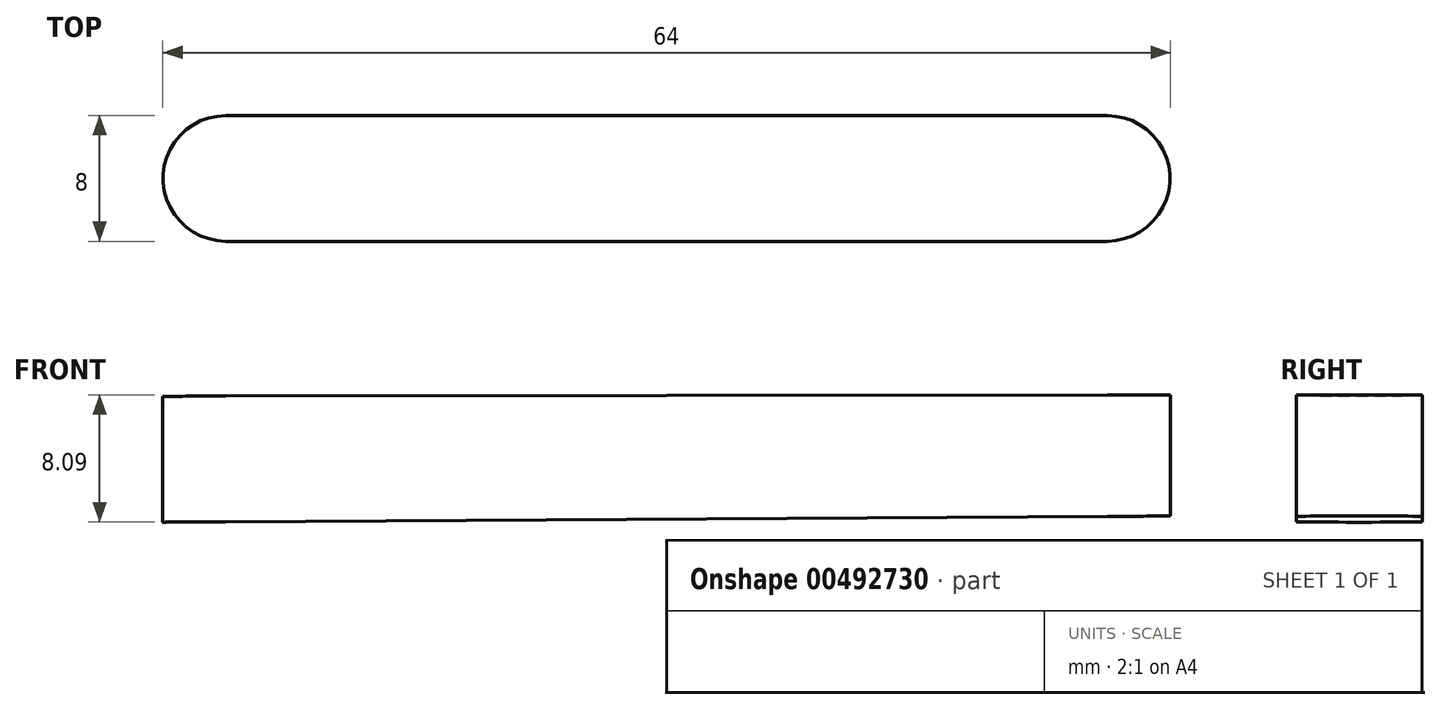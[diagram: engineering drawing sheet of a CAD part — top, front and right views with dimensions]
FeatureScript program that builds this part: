
annotation { "Feature Type Name" : "Feature", "Feature Type Description" : "" }
export const myFeature = defineFeature(function(context is Context, id is Id, definition is map)
    precondition{}
    {
        {
            var Q0;
            Q0=qCreatedBy(makeId("Front.planeOp"),FACE);
            var sketch = newSketch(context, id + "F0", { "sketchPlane" : qUnion([Q0])});
            skLineSegment(sketch, "E0.left", {"start": v(-14.73, 0) * mm, "end": v(-14.73, -7.7) * mm});
            skLineSegment(sketch, "E0.right", {"start": v(-78.73, -0.1) * mm, "end": v(-78.73, -8.1) * mm});
            skPoint(sketch, "E1", {"position": v(-14.73, 0) * mm});
            skPoint(sketch, "E2", {"position": v(-78.73, -0.1) * mm});
            skLineSegment(sketch, "E3", {"start": v(-78.73, -0.1) * mm, "end": v(-62.73, -0.07) * mm});
            skLineSegment(sketch, "E4", {"start": v(-78.73, -8.1) * mm, "end": v(-14.73, -7.7) * mm});
            skLineSegment(sketch, "E5", {"start": v(-46.73, -0.05) * mm, "end": v(-46.68, -7.9) * mm});
            skLineSegment(sketch, "E6", {"start": v(-46.73, -0.05) * mm, "end": v(-30.73, -0.02) * mm});
            skLineSegment(sketch, "E7", {"start": v(-46.68, -7.9) * mm, "end": v(-46.68, -7.9) * mm});
            skLineSegment(sketch, "E8", {"start": v(-62.73, 0) * mm, "end": v(-62.72, -8) * mm});
            skPoint(sketch, "E8.startSnap0", {"position": v(-62.73, -0.07) * mm});
            skLineSegment(sketch, "E9", {"start": v(-62.73, -0.07) * mm, "end": v(-46.73, -0.05) * mm});
            skLineSegment(sketch, "E10", {"start": v(-30.73, -0.02) * mm, "end": v(-14.73, 0) * mm});
            skLineSegment(sketch, "E11", {"start": v(-70.73, -0.08) * mm, "end": v(-70.72, -8.04) * mm});
            skLineSegment(sketch, "E12", {"start": v(-54.73, -0.06) * mm, "end": v(-54.72, -7.95) * mm});
            skLineSegment(sketch, "E13", {"start": v(-30.73, -0.02) * mm, "end": v(-30.72, -7.8) * mm});
            skLineSegment(sketch, "E14", {"start": v(-38.73, -0.03) * mm, "end": v(-38.72, -7.85) * mm});
            skLineSegment(sketch, "E15", {"start": v(-22.73, -0.01) * mm, "end": v(-22.72, -7.75) * mm});
            skPoint(sketch, "E16", {"position": v(-70.73, -0.08) * mm});
            skPoint(sketch, "E17", {"position": v(-62.73, 0) * mm});
            skPoint(sketch, "E18", {"position": v(-54.73, -0.06) * mm});
            skPoint(sketch, "E19", {"position": v(-46.73, -0.05) * mm});
            skPoint(sketch, "E20", {"position": v(-38.73, -0.03) * mm});
            skPoint(sketch, "E21", {"position": v(-30.73, -0.02) * mm});
            skPoint(sketch, "E22", {"position": v(-22.73, -0.01) * mm});
            skSolve(sketch);
        }
        {
            var Q0;
            {var subQ0=sQuery(id+"F0.wireOp",EDGE,"cbd0fde2-b0bf-40bd-90c5-5901da540db1");var subQ1=sQuery(id+"F0.wireOp",EDGE,"E0.right");var subQ2=makeQuery(id+"F0.imprint","INTERSECT",VERTEX,{"derivedFrom":[subQ1,subQ0]});Q0=makeQuery(id+"F0.imprint","IMPRINT",FACE,{"disambiguationData":[TD([[makeQuery(id+"F0.imprint","IMPRINT",EDGE,{"disambiguationData":[TD([[subQ2,1.0]])],"derivedFrom":subQ1}),1.0]])]});}
            var Q1;
            {var subQ0=sQuery(id+"F0.wireOp",EDGE,"vCAPm1U1-NcBP-Hxi9-G9nz-eafg9Nj5RmCp");var subQ1=sQuery(id+"F0.wireOp",EDGE,"fk9a7EGv-8zqn-m2js-nKql-ahyp9wCgeFvH");var subQ2=makeQuery(id+"F0.imprint","INTERSECT",VERTEX,{"derivedFrom":[subQ1,subQ0]});Q1=makeQuery(id+"F0.imprint","IMPRINT",FACE,{"disambiguationData":[TD([[makeQuery(id+"F0.imprint","IMPRINT",EDGE,{"disambiguationData":[TD([[subQ2,-1.0]])],"derivedFrom":subQ1}),1.0]])]});}
            var Q2;
            {var subQ0=sQuery(id+"F0.wireOp",EDGE,"vCAPm1U1-NcBP-Hxi9-G9nz-eafg9Nj5RmCp");var subQ1=sQuery(id+"F0.wireOp",EDGE,"fk9a7EGv-8zqn-m2js-nKql-ahyp9wCgeFvH");var subQ2=makeQuery(id+"F0.imprint","INTERSECT",VERTEX,{"derivedFrom":[subQ1,subQ0]});Q2=makeQuery(id+"F0.imprint","IMPRINT",FACE,{"disambiguationData":[TD([[makeQuery(id+"F0.imprint","IMPRINT",EDGE,{"disambiguationData":[TD([[subQ2,-1.0]])],"derivedFrom":subQ1}),-1.0]])]});}
            var Q3;
            {var subQ0=sQuery(id+"F0.wireOp",EDGE,"C6XTvMNN-qSv2-rY8C-A6cv-MqWbsheSMjOx");var subQ1=sQuery(id+"F0.wireOp",EDGE,"fk9a7EGv-8zqn-m2js-nKql-ahyp9wCgeFvH");var subQ2=makeQuery(id+"F0.imprint","INTERSECT",VERTEX,{"derivedFrom":[subQ1,subQ0]});Q3=makeQuery(id+"F0.imprint","IMPRINT",FACE,{"disambiguationData":[TD([[makeQuery(id+"F0.imprint","IMPRINT",EDGE,{"disambiguationData":[TD([[subQ2,-1.0]])],"derivedFrom":subQ1}),1.0]])]});}
            var Q4;
            {var subQ0=sQuery(id+"F0.wireOp",EDGE,"0sJRDTbM-qxML-Fhed-qwCp-Eef6TRP1OfcN");var subQ1=sQuery(id+"F0.wireOp",EDGE,"E0.right");var subQ2=makeQuery(id+"F0.imprint","INTERSECT",VERTEX,{"derivedFrom":[subQ1,subQ0]});Q4=makeQuery(id+"F0.imprint","IMPRINT",FACE,{"disambiguationData":[TD([[makeQuery(id+"F0.imprint","IMPRINT",EDGE,{"disambiguationData":[TD([[subQ2,-1.0]])],"derivedFrom":subQ1}),1.0]])]});}
            var Q5;
            {var subQ3=sQuery(id+"F0.wireOp",EDGE,"LIEBb9lc-Vvww-VdWq-rq3m-nkQYKgmDdQ5W");var subQ5=sQuery(id+"F0.wireOp",EDGE,"28611474-2130-4277-93cf-13f55d4a7ebc");var subQ7=makeQuery(id+"F0.imprint","INTERSECT",VERTEX,{"derivedFrom":[subQ5,subQ3]});Q5=makeQuery(id+"F0.imprint","IMPRINT",FACE,{"disambiguationData":[TD([[makeQuery(id+"F0.imprint","IMPRINT",EDGE,{"disambiguationData":[TD([[subQ7,1.0]])],"derivedFrom":subQ3}),-1.0]])]});}
            var Q6;
            {var subQ1=sQuery(id+"F0.wireOp",EDGE,"fk9a7EGv-8zqn-m2js-nKql-ahyp9wCgeFvH");var subQ3=sQuery(id+"F0.wireOp",EDGE,"LIEBb9lc-Vvww-VdWq-rq3m-nkQYKgmDdQ5W");var subQ4=makeQuery(id+"F0.imprint","INTERSECT",VERTEX,{"derivedFrom":[subQ1,subQ3]});Q6=makeQuery(id+"F0.imprint","IMPRINT",FACE,{"disambiguationData":[TD([[makeQuery(id+"F0.imprint","IMPRINT",EDGE,{"disambiguationData":[TD([[subQ4,-1.0]])],"derivedFrom":subQ1}),-1.0]])]});}
            var Q7;
            {var subQ5=sQuery(id+"F0.wireOp",EDGE,"FogfJIDQ-61h2-FOwa-hR6e-gylFLFGPtxlj");Q7=makeQuery(id+"F0.imprint","IMPRINT",FACE,{"disambiguationData":[TD([[makeQuery(id+"F0.imprint","IMPRINT",EDGE,{"derivedFrom":subQ5}),1.0]])]});}
            var Q8;
            {var subQ3=sQuery(id+"F0.wireOp",EDGE,"vPtWs0Qi-DTHT-ycth-RI1T-cvgh728iN0rk");var subQ5=sQuery(id+"F0.wireOp",EDGE,"0f361283-31ae-48d5-a095-6cd1e26f46ad");var subQ7=makeQuery(id+"F0.imprint","INTERSECT",VERTEX,{"derivedFrom":[subQ5,subQ3]});Q8=makeQuery(id+"F0.imprint","IMPRINT",FACE,{"disambiguationData":[TD([[makeQuery(id+"F0.imprint","IMPRINT",EDGE,{"disambiguationData":[TD([[subQ7,1.0]])],"derivedFrom":subQ5}),-1.0]])]});}
            var Q9;
            {var subQ3=sQuery(id+"F0.wireOp",EDGE,"dbe129d0-8bf3-4541-82ca-7bb60f21fa00");var subQ5=sQuery(id+"F0.wireOp",EDGE,"vPtWs0Qi-DTHT-ycth-RI1T-cvgh728iN0rk");var subQ6=makeQuery(id+"F0.imprint","INTERSECT",VERTEX,{"derivedFrom":[subQ3,subQ5]});Q9=makeQuery(id+"F0.imprint","IMPRINT",FACE,{"disambiguationData":[TD([[makeQuery(id+"F0.imprint","IMPRINT",EDGE,{"disambiguationData":[TD([[subQ6,-1.0]])],"derivedFrom":subQ5}),-1.0]])]});}
            var Q10;
            {var subQ3=sQuery(id+"F0.wireOp",EDGE,"vPtWs0Qi-DTHT-ycth-RI1T-cvgh728iN0rk");var subQ5=sQuery(id+"F0.wireOp",EDGE,"0f361283-31ae-48d5-a095-6cd1e26f46ad");var subQ6=makeQuery(id+"F0.imprint","INTERSECT",VERTEX,{"derivedFrom":[subQ5,subQ3]});Q10=makeQuery(id+"F0.imprint","IMPRINT",FACE,{"disambiguationData":[TD([[makeQuery(id+"F0.imprint","IMPRINT",EDGE,{"disambiguationData":[TD([[subQ6,-1.0]])],"derivedFrom":subQ5}),1.0]])]});}
            var Q11;
            {var subQ5=sQuery(id+"F0.wireOp",EDGE,"zsZEawIq-kxFd-f7ct-tQDc-zZMPCkPWAenP");Q11=makeQuery(id+"F0.imprint","IMPRINT",FACE,{"disambiguationData":[TD([[makeQuery(id+"F0.imprint","IMPRINT",EDGE,{"derivedFrom":subQ5}),1.0]])]});}
            var Q12;
            {var subQ0=sQuery(id+"F0.wireOp",EDGE,"xvlKTwpL-h0JT-CeHc-zemS-WiL0mXiXVSER");var subQ5=sQuery(id+"F0.wireOp",EDGE,"0f361283-31ae-48d5-a095-6cd1e26f46ad");var subQ7=makeQuery(id+"F0.imprint","INTERSECT",VERTEX,{"derivedFrom":[subQ5,subQ0]});Q12=makeQuery(id+"F0.imprint","IMPRINT",FACE,{"disambiguationData":[TD([[makeQuery(id+"F0.imprint","IMPRINT",EDGE,{"disambiguationData":[TD([[subQ7,-1.0]])],"derivedFrom":subQ5}),-1.0]])]});}
            var Q13;
            {var subQ0=sQuery(id+"F0.wireOp",EDGE,"xvlKTwpL-h0JT-CeHc-zemS-WiL0mXiXVSER");var subQ1=sQuery(id+"F0.wireOp",EDGE,"0f361283-31ae-48d5-a095-6cd1e26f46ad");var subQ2=makeQuery(id+"F0.imprint","INTERSECT",VERTEX,{"derivedFrom":[subQ1,subQ0]});Q13=makeQuery(id+"F0.imprint","IMPRINT",FACE,{"disambiguationData":[TD([[makeQuery(id+"F0.imprint","IMPRINT",EDGE,{"disambiguationData":[TD([[subQ2,-1.0]])],"derivedFrom":subQ1}),1.0]])]});}
            var Q14;
            {var subQ0=sQuery(id+"F0.wireOp",EDGE,"d530a60e-0b21-4390-a23b-4bf93617f922");var subQ1=sQuery(id+"F0.wireOp",EDGE,"E0.left");var subQ2=makeQuery(id+"F0.imprint","INTERSECT",VERTEX,{"derivedFrom":[subQ1,subQ0]});Q14=makeQuery(id+"F0.imprint","IMPRINT",FACE,{"disambiguationData":[TD([[makeQuery(id+"F0.imprint","IMPRINT",EDGE,{"disambiguationData":[TD([[subQ2,-1.0]])],"derivedFrom":subQ1}),-1.0]])]});}
            var Q15;
            {var subQ0=sQuery(id+"F0.wireOp",EDGE,"E0.left");var subQ1=sQuery(id+"F0.wireOp",EDGE,"E0.top");var subQ2=makeQuery(id+"F0.imprint","INTERSECT",VERTEX,{"derivedFrom":[subQ1,subQ0]});Q15=makeQuery(id+"F0.imprint","IMPRINT",FACE,{"disambiguationData":[TD([[makeQuery(id+"F0.imprint","IMPRINT",EDGE,{"disambiguationData":[TD([[subQ2,-1.0]])],"derivedFrom":subQ1}),-1.0]])]});}
            var Q16;
            {var subQ3=sQuery(id+"F0.wireOp",EDGE,"E11");Q16=makeQuery(id+"F0.imprint","IMPRINT",FACE,{"disambiguationData":[TD([[makeQuery(id+"F0.imprint","IMPRINT",EDGE,{"derivedFrom":subQ3}),1.0]])]});}
            var Q17;
            {var subQ3=sQuery(id+"F0.wireOp",EDGE,"E12");Q17=makeQuery(id+"F0.imprint","IMPRINT",FACE,{"disambiguationData":[TD([[makeQuery(id+"F0.imprint","IMPRINT",EDGE,{"derivedFrom":subQ3}),-1.0]])]});}
            var Q18;
            {var subQ0=sQuery(id+"F0.wireOp",EDGE,"E5");Q18=makeQuery(id+"F0.imprint","IMPRINT",FACE,{"disambiguationData":[TD([[makeQuery(id+"F0.imprint","IMPRINT",EDGE,{"derivedFrom":subQ0}),-1.0]])]});}
            var Q19;
            {var subQ0=sQuery(id+"F0.wireOp",EDGE,"E13");Q19=makeQuery(id+"F0.imprint","IMPRINT",FACE,{"disambiguationData":[TD([[makeQuery(id+"F0.imprint","IMPRINT",EDGE,{"derivedFrom":subQ0}),-1.0]])]});}
            var Q20;
            {var subQ0=sQuery(id+"F0.wireOp",EDGE,"E13");Q20=makeQuery(id+"F0.imprint","IMPRINT",FACE,{"disambiguationData":[TD([[makeQuery(id+"F0.imprint","IMPRINT",EDGE,{"derivedFrom":subQ0}),1.0]])]});}
            var Q21;
            {var subQ0=sQuery(id+"F0.wireOp",EDGE,"E5");Q21=makeQuery(id+"F0.imprint","IMPRINT",FACE,{"disambiguationData":[TD([[makeQuery(id+"F0.imprint","IMPRINT",EDGE,{"derivedFrom":subQ0}),1.0]])]});}
            extrude(context, id + "F1", {"entities" : qUnion([Q0, Q1, Q2, Q3, Q4, Q5, Q6, Q7, Q8, Q9, Q10, Q11, Q12, Q13, Q14, Q15, Q16, Q17, Q18, Q19, Q20, Q21]), "endBound" : BoundingType.SYMMETRIC, "depth" : 8 * mm});
        }
        {
            var Q0;
            Q0=makeQuery(id+"F1.opExtrude","CAP_EDGE",EDGE,{"disambiguationData":[OSD([sQuery(id+"F0.wireOp",EDGE,"E0.right")])],"isStart":true});
            var Q1;
            Q1=makeQuery(id+"F1.opExtrude","CAP_EDGE",EDGE,{"disambiguationData":[OSD([sQuery(id+"F0.wireOp",EDGE,"E0.right")])],"isStart":false});
            var Q2;
            Q2=makeQuery(id+"F1.opExtrude","CAP_EDGE",EDGE,{"disambiguationData":[OSD([sQuery(id+"F0.wireOp",EDGE,"E0.left")])],"isStart":true});
            var Q3;
            Q3=makeQuery(id+"F1.opExtrude","CAP_EDGE",EDGE,{"disambiguationData":[OSD([sQuery(id+"F0.wireOp",EDGE,"E0.left")])],"isStart":false});
            fillet(context, id + "F2", {"entities" : qUnion([Q0, Q1, Q2, Q3]), "radius" : 4 * mm, "tangentPropagation" : true, "allowEdgeOverflow" : false});
        }
    });
